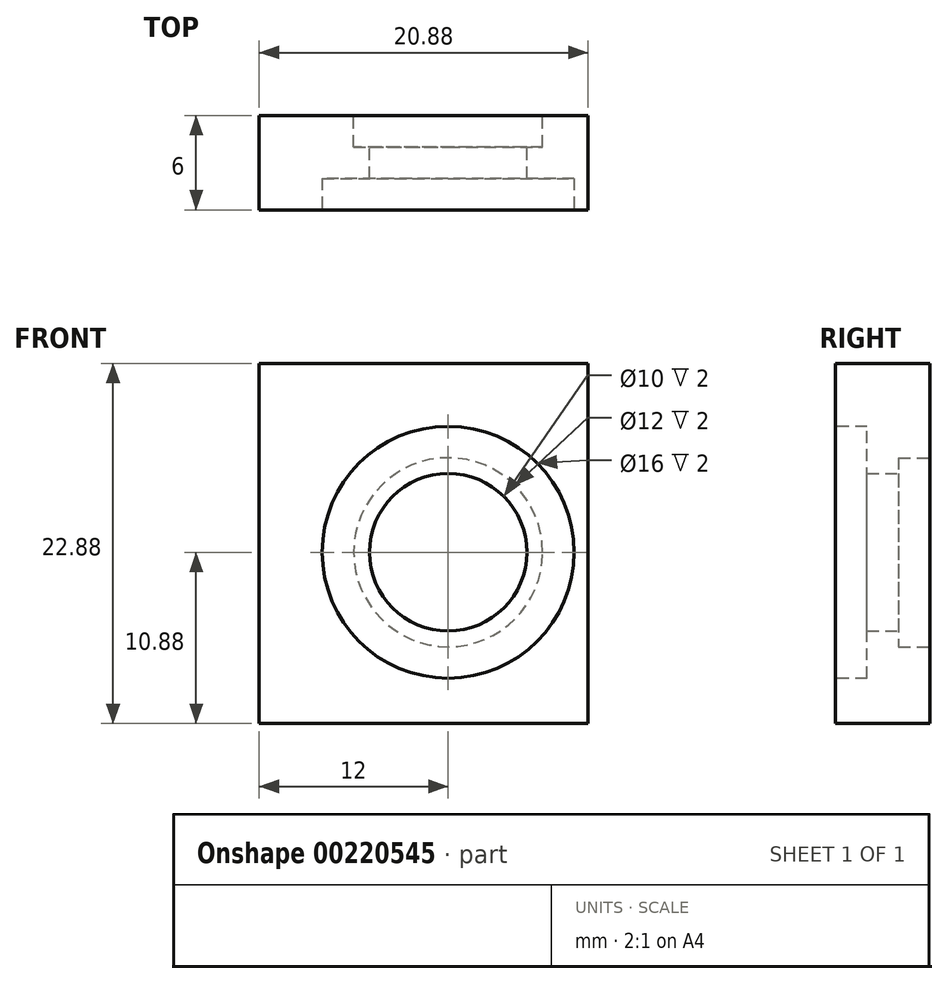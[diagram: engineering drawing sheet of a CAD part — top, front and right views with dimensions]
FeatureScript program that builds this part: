
annotation { "Feature Type Name" : "Feature", "Feature Type Description" : "" }
export const myFeature = defineFeature(function(context is Context, id is Id, definition is map)
    precondition{}
    {
        {
            var Q0;
            Q0=qCreatedBy(makeId("Front.planeOp"),FACE);
            var sketch = newSketch(context, id + "F0", { "sketchPlane" : qUnion([Q0])});
            skLineSegment(sketch, "E0.right", {"start": v(67, 15) * mm, "end": v(67, -15) * mm});
            skPoint(sketch, "E0.middle", {"position": v(0, 0) * mm});
            skCircle(sketch, "E1", {"center": v(40, 10) * mm, "radius": 4.5 * mm});
            skCircle(sketch, "E2", {"center": v(60, 10) * mm, "radius": 4.5 * mm});
            skCircle(sketch, "E3", {"center": v(60, -10) * mm, "radius": 4.5 * mm});
            skCircle(sketch, "E4", {"center": v(40, -10) * mm, "radius": 4.5 * mm});
            skCircle(sketch, "E5", {"center": v(0, 11) * mm, "radius": 1.5 * mm});
            skCircle(sketch, "E6", {"center": v(0, -11) * mm, "radius": 1.5 * mm});
            skCircle(sketch, "E7", {"center": v(14, 0) * mm, "radius": 1.5 * mm});
            skCircle(sketch, "E8", {"center": v(-14, 0) * mm, "radius": 1.5 * mm});
            skPoint(sketch, "E9.endSnap0", {"position": v(0, 14) * mm});
            skLineSegment(sketch, "E10", {"start": v(-12.5, 14) * mm, "end": v(-12.5, 16) * mm});
            skLineSegment(sketch, "E11", {"start": v(-12.5, -14) * mm, "end": v(-12.5, -16) * mm});
            skLineSegment(sketch, "E12", {"start": v(12.5, 14) * mm, "end": v(12.5, 16) * mm});
            skLineSegment(sketch, "E13", {"start": v(12.5, -14) * mm, "end": v(12.5, -16) * mm});
            skLineSegment(sketch, "E14.0", {"start": v(-22.5, 14) * mm, "end": v(-22.5, 16) * mm});
            skLineSegment(sketch, "E15.0", {"start": v(22.5, 14) * mm, "end": v(22.5, 16) * mm});
            skLineSegment(sketch, "E16.0", {"start": v(-22.5, -14) * mm, "end": v(-22.5, -16) * mm});
            skLineSegment(sketch, "E17.0", {"start": v(22.5, -14) * mm, "end": v(22.5, -16) * mm});
            skLineSegment(sketch, "E18.trimOffspring", {"start": v(-22.5, 16) * mm, "end": v(-12.5, 16) * mm});
            skLineSegment(sketch, "E19.trimOffspring", {"start": v(-22.5, 14) * mm, "end": v(-12.5, 14) * mm});
            skLineSegment(sketch, "E20.trimOffspring", {"start": v(12.5, 16) * mm, "end": v(22.5, 16) * mm});
            skLineSegment(sketch, "E21.trimOffspring", {"start": v(12.5, 14) * mm, "end": v(22.5, 14) * mm});
            skLineSegment(sketch, "E22.trimOffspring", {"start": v(-22.5, -14) * mm, "end": v(-12.5, -14) * mm});
            skLineSegment(sketch, "E23.trimOffspring", {"start": v(-22.5, -16) * mm, "end": v(-12.5, -16) * mm});
            skLineSegment(sketch, "E24.trimOffspring", {"start": v(12.5, -14) * mm, "end": v(22.5, -14) * mm});
            skLineSegment(sketch, "E25.trimOffspring", {"start": v(12.5, -16) * mm, "end": v(22.5, -16) * mm});
            skLineSegment(sketch, "E26", {"start": v(-93, 17) * mm, "end": v(65, 17) * mm});
            skLineSegment(sketch, "E27", {"start": v(-93, -17) * mm, "end": v(65, -17) * mm});
            skCircle(sketch, "E28", {"center": v(-83, 10) * mm, "radius": 4.5 * mm});
            skCircle(sketch, "E29", {"center": v(-83, -10) * mm, "radius": 4.5 * mm});
            skCircle(sketch, "E30", {"center": v(-63, 10) * mm, "radius": 4.5 * mm});
            skCircle(sketch, "E31", {"center": v(-63, -10) * mm, "radius": 4.5 * mm});
            skLineSegment(sketch, "E32.0", {"start": v(-95, 15) * mm, "end": v(-95, -15) * mm});
            skLineSegment(sketch, "E33.0", {"start": v(-91.25, 17) * mm, "end": v(-91.25, -17) * mm, "construction": true});
            skLineSegment(sketch, "E34", {"start": v(-63, 10) * mm, "end": v(-95, 10) * mm, "construction": true});
            skLineSegment(sketch, "E35", {"start": v(-63, -10) * mm, "end": v(-95, -10) * mm, "construction": true});
            skLineSegment(sketch, "E36", {"start": v(-83, 17) * mm, "end": v(-83, -17) * mm, "construction": true});
            skLineSegment(sketch, "E37", {"start": v(-14, 0) * mm, "end": v(-95, 0) * mm, "construction": true});
            skLineSegment(sketch, "E38.0", {"start": v(-14, 3) * mm, "end": v(-95, 3) * mm, "construction": true});
            skLineSegment(sketch, "E39.0", {"start": v(-14, -3) * mm, "end": v(-95, -3) * mm, "construction": true});
            skLineSegment(sketch, "E40", {"start": v(-74.75, 10) * mm, "end": v(-74.75, -10) * mm, "construction": true});
            skCircle(sketch, "E41", {"center": v(-91.25, 3) * mm, "radius": 1.5 * mm, "construction": true});
            skCircle(sketch, "E42", {"center": v(-91.25, -3) * mm, "radius": 1.5 * mm, "construction": true});
            skCircle(sketch, "E43", {"center": v(-74.75, 3) * mm, "radius": 1.5 * mm, "construction": true});
            skCircle(sketch, "E44", {"center": v(-74.75, -3) * mm, "radius": 1.5 * mm, "construction": true});
            skPoint(sketch, "E45.visualSharp", {"position": v(-95, 17) * mm});
            skArc(sketch, "E45.filletArc", {"start": v(-93, 17) * mm, "mid": v(-94.41, 16.41) * mm, "end": v(-95, 15) * mm});
            skPoint(sketch, "E46.visualSharp", {"position": v(-95, -17) * mm});
            skArc(sketch, "E46.filletArc", {"start": v(-95, -15) * mm, "mid": v(-94.41, -16.41) * mm, "end": v(-93, -17) * mm});
            skPoint(sketch, "E47.visualSharp", {"position": v(67, 17) * mm});
            skArc(sketch, "E47.filletArc", {"start": v(67, 15) * mm, "mid": v(66.41, 16.41) * mm, "end": v(65, 17) * mm});
            skPoint(sketch, "E48.visualSharp", {"position": v(67, -17) * mm});
            skArc(sketch, "E48.filletArc", {"start": v(65, -17) * mm, "mid": v(66.41, -16.41) * mm, "end": v(67, -15) * mm});
            skSolve(sketch);
        }
        {
            var Q0;
            Q0=makeQuery(id+"F0.imprint","IMPRINT",FACE,{"disambiguationData":[TD([[makeQuery(id+"F0.imprint","IMPRINT",EDGE,{"derivedFrom":sQuery(id+"F0.wireOp",EDGE,"E0.right")}),-1.0]])]});
            var sketch = newSketch(context, id + "F1", { "sketchPlane" : qUnion([Q0])});
            skCircle(sketch, "E49.0", {"center": v(-83, 10) * mm, "radius": 4.5 * mm});
            skCircle(sketch, "E50.0", {"center": v(-63, 10) * mm, "radius": 4.5 * mm});
            skCircle(sketch, "E51.0", {"center": v(-63, -10) * mm, "radius": 4.5 * mm});
            skCircle(sketch, "E52.0", {"center": v(-83, -10) * mm, "radius": 4.5 * mm});
            skPoint(sketch, "E53.0", {"position": v(-95, 17) * mm});
            skPoint(sketch, "E54.0", {"position": v(-95, -17) * mm});
            skLineSegment(sketch, "E55", {"start": v(-95, 17) * mm, "end": v(-95, -17) * mm});
            skLineSegment(sketch, "E56", {"start": v(-95, -17) * mm, "end": v(-53.24, -17) * mm});
            skLineSegment(sketch, "E57", {"start": v(-53.24, 17) * mm, "end": v(-53.24, -17) * mm});
            skLineSegment(sketch, "E58", {"start": v(-53.24, 17) * mm, "end": v(-95, 17) * mm});
            skSolve(sketch);
        }
        {
            var Q0;
            Q0=makeQuery(id+"F1.imprint","IMPRINT",FACE,{"disambiguationData":[TD([[makeQuery(id+"F1.imprint","IMPRINT",EDGE,{"derivedFrom":sQuery(id+"F1.wireOp",EDGE,"E49.0")}),-1.0]])]});
            var sketch = newSketch(context, id + "F2", { "sketchPlane" : qUnion([Q0])});
            skLineSegment(sketch, "E59.0", {"start": v(-53.24, 17) * mm, "end": v(-95, 17) * mm});
            skLineSegment(sketch, "E60.0", {"start": v(-95, 17) * mm, "end": v(-95, -17) * mm});
            skLineSegment(sketch, "E61.0", {"start": v(-53.24, 17) * mm, "end": v(-53.24, -17) * mm});
            skLineSegment(sketch, "E62.0", {"start": v(-95, -17) * mm, "end": v(-53.24, -17) * mm});
            skPoint(sketch, "E63.0", {"position": v(-63, -10) * mm});
            skPoint(sketch, "E64.0", {"position": v(-63, 10) * mm});
            skPoint(sketch, "E65.0", {"position": v(-83, 10) * mm});
            skPoint(sketch, "E66.0", {"position": v(-83, -10) * mm});
            skLineSegment(sketch, "E67.0", {"start": v(-53.24, 22) * mm, "end": v(-95, 22) * mm});
            skLineSegment(sketch, "E68", {"start": v(-53.24, 22) * mm, "end": v(-53.24, 17) * mm});
            skLineSegment(sketch, "E69", {"start": v(-95, 22) * mm, "end": v(-95, 17) * mm});
            skLineSegment(sketch, "E70", {"start": v(-74.12, 22) * mm, "end": v(-74.12, -17) * mm});
            skLineSegment(sketch, "E71", {"start": v(-74.12, -17) * mm, "end": v(-74.12, 2.5) * mm});
            skLineSegment(sketch, "E72", {"start": v(-74.12, 2.5) * mm, "end": v(-95, 2.5) * mm});
            skLineSegment(sketch, "E73", {"start": v(-74.12, -0.88) * mm, "end": v(-95, -0.88) * mm});
            skSolve(sketch);
        }
        {
            var Q0;
            Q0=makeQuery(id+"F2.imprint","IMPRINT",FACE,{"disambiguationData":[TD([[makeQuery(id+"F2.imprint","IMPRINT",EDGE,{"derivedFrom":makeQuery(id+"F1.imprint","IMPRINT",EDGE,{"derivedFrom":sQuery(id+"F1.wireOp",EDGE,"E49.0")})}),1.0]])]});
            var Q1;
            {var subQ0=sQuery(id+"F2.wireOp",EDGE,"E72");Q1=makeQuery(id+"F2.imprint","IMPRINT",FACE,{"disambiguationData":[TD([[makeQuery(id+"F2.imprint","IMPRINT",EDGE,{"derivedFrom":subQ0}),-1.0]])]});}
            var Q2;
            {var subQ0=sQuery(id+"F2.wireOp",EDGE,"E69");Q2=makeQuery(id+"F2.imprint","IMPRINT",FACE,{"disambiguationData":[TD([[makeQuery(id+"F2.imprint","IMPRINT",EDGE,{"derivedFrom":subQ0}),1.0]])]});}
            var Q3;
            {var subQ0=sQuery(id+"F2.wireOp",EDGE,"E72");Q3=makeQuery(id+"F2.imprint","IMPRINT",FACE,{"disambiguationData":[TD([[makeQuery(id+"F2.imprint","IMPRINT",EDGE,{"derivedFrom":subQ0}),1.0]])]});}
            var Q4;
            {var subQ1=makeQuery(id+"F1.imprint","IMPRINT",EDGE,{"derivedFrom":makeQuery(id+"F0.imprint","IMPRINT",EDGE,{"derivedFrom":sQuery(id+"F0.wireOp",EDGE,"E45.filletArc")})});Q4=makeQuery(id+"F2.imprint","IMPRINT",FACE,{"disambiguationData":[TD([[makeQuery(id+"F2.imprint","IMPRINT",EDGE,{"derivedFrom":subQ1}),-1.0]])]});}
            extrude(context, id + "F3", {"entities" : qUnion([Q0, Q1, Q2, Q3, Q4]), "depth" : 6 * mm});
        }
        {
            var Q0;
            Q0=sQuery(id+"F2.wireOp",VERTEX,"E64.0");
            var Q1;
            Q1=sQuery(id+"F2.wireOp",VERTEX,"E65.0");
            var Q2;
            Q2=sQuery(id+"F2.wireOp",VERTEX,"E66.0");
            var Q3;
            Q3=sQuery(id+"F2.wireOp",VERTEX,"E63.0");
            var Q4;
            Q4=makeQuery(id+"F3.opExtrude","SWEPT_BODY",BODY,{"disambiguationData":[OSD([sQuery(id+"F0.wireOp",EDGE,"E45.filletArc"),sQuery(id+"F0.wireOp",EDGE,"E46.filletArc"),sQuery(id+"F2.wireOp",EDGE,"E59.0"),sQuery(id+"F2.wireOp",EDGE,"E60.0"),sQuery(id+"F2.wireOp",EDGE,"E61.0"),sQuery(id+"F2.wireOp",EDGE,"E62.0")])]});
            hole(context, id + "F4", {"style" : HoleStyle.C_BORE, "endStyle" : HoleEndStyle.BLIND, "oppositeDirection" : true, "holeDiameter" : 10 * mm, "cBoreDiameter" : 12 * mm, "cBoreDepth" : 2 * mm, "holeDepth" : 4 * mm, "tappedDepth" : 12 * mm, "tapClearance" : 3, "locations" : qUnion([Q0, Q1, Q2, Q3]), "scope" : qUnion([Q4])});
        }
        {
            var Q0;
            Q0=makeQuery(id+"F3.opExtrude","CAP_FACE",FACE,{"disambiguationData":[OSD([sQuery(id+"F2.wireOp",EDGE,"E60.0"),sQuery(id+"F2.wireOp",EDGE,"E67.0"),sQuery(id+"F2.wireOp",EDGE,"E69"),sQuery(id+"F2.wireOp",EDGE,"E70"),sQuery(id+"F2.wireOp",EDGE,"E73")])],"isStart":false});
            var sketch = newSketch(context, id + "F5", { "sketchPlane" : qUnion([Q0])});
            skPoint(sketch, "E74.0", {"position": v(-83, 10) * mm});
            skSolve(sketch);
        }
        {
            var Q0;
            Q0=sQuery(id+"F5.wireOp",VERTEX,"E74.0");
            var Q1;
            Q1=makeQuery(id+"F3.opExtrude","SWEPT_BODY",BODY,{"disambiguationData":[OSD([sQuery(id+"F2.wireOp",EDGE,"E60.0"),sQuery(id+"F2.wireOp",EDGE,"E67.0"),sQuery(id+"F2.wireOp",EDGE,"E69"),sQuery(id+"F2.wireOp",EDGE,"E70"),sQuery(id+"F2.wireOp",EDGE,"E73")])]});
            hole(context, id + "F6", {"style" : HoleStyle.C_BORE, "endStyle" : HoleEndStyle.BLIND, "holeDiameter" : 9 * mm, "cBoreDiameter" : 16 * mm, "cBoreDepth" : 2 * mm, "holeDepth" : 6 * mm, "tappedDepth" : 12 * mm, "tapClearance" : 3, "locations" : qUnion([Q0]), "scope" : qUnion([Q1])});
        }
    });
